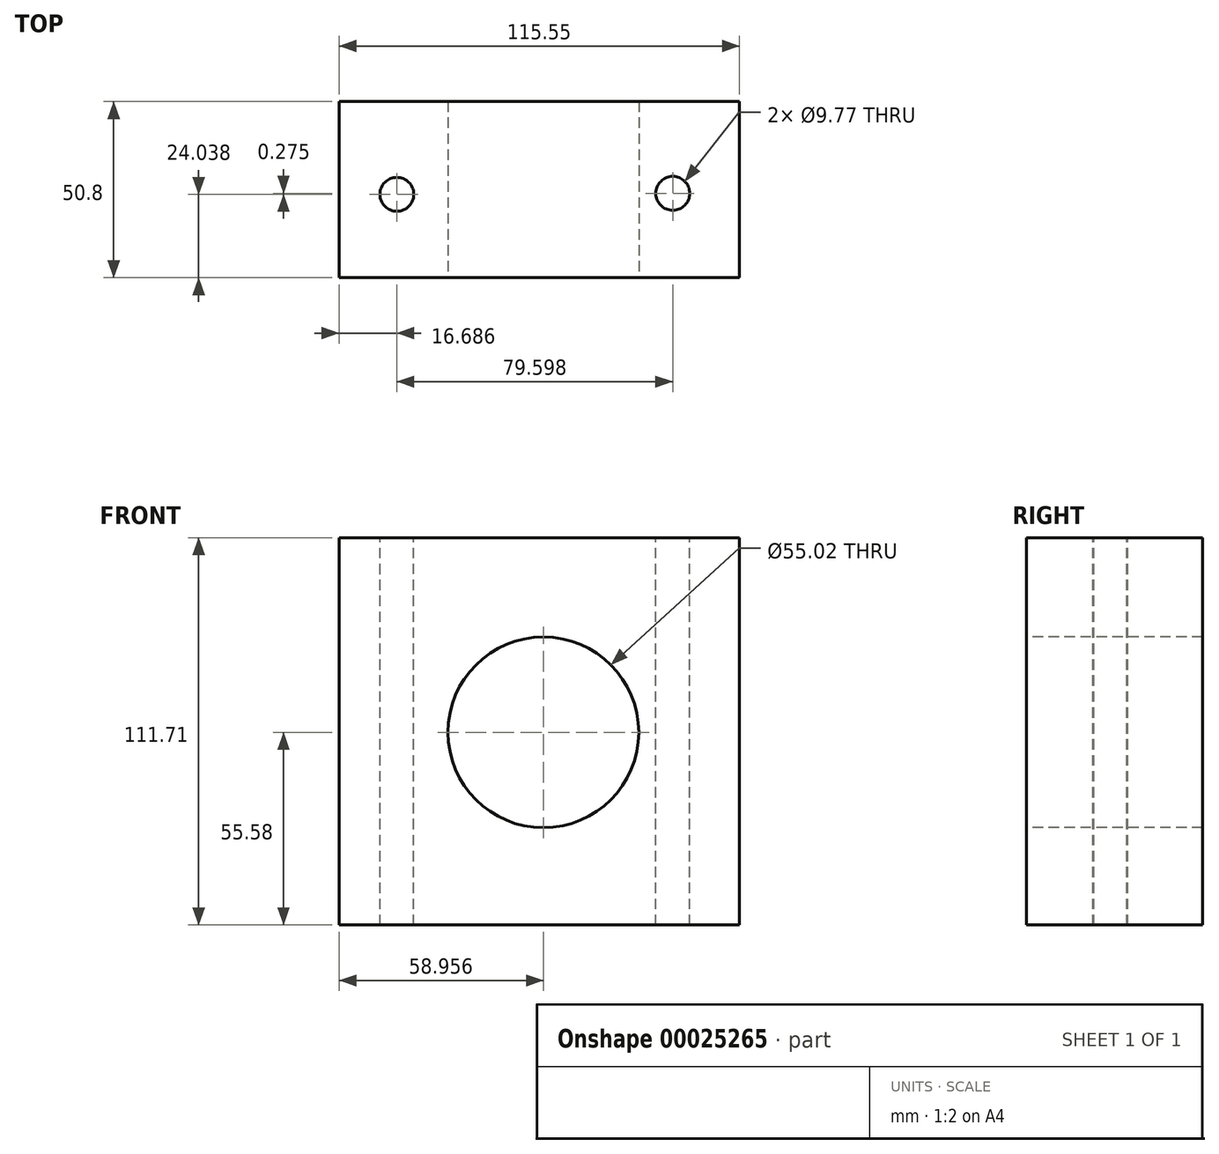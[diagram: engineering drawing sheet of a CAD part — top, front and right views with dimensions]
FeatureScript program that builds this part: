
annotation { "Feature Type Name" : "Feature", "Feature Type Description" : "" }
export const myFeature = defineFeature(function(context is Context, id is Id, definition is map)
    precondition{}
    {
        {
            var Q0;
            Q0=qCreatedBy(makeId("Front.planeOp"),FACE);
            var sketch = newSketch(context, id + "F0", { "sketchPlane" : qUnion([Q0])});
            skLineSegment(sketch, "E0", {"start": v(-76.3, 56.13) * mm, "end": v(-76.3, -55.58) * mm});
            skLineSegment(sketch, "E1", {"start": v(-76.3, -55.58) * mm, "end": v(39.25, -55.58) * mm});
            skLineSegment(sketch, "E2", {"start": v(39.25, -55.58) * mm, "end": v(39.25, 56.13) * mm});
            skLineSegment(sketch, "E3", {"start": v(39.25, 56.13) * mm, "end": v(-76.3, 56.13) * mm});
            skSolve(sketch);
        }
        {
            var Q0;
            Q0=makeQuery(id+"F0.imprint","IMPRINT",FACE,{"disambiguationData":[TD([[makeQuery(id+"F0.imprint","IMPRINT",EDGE,{"derivedFrom":sQuery(id+"F0.wireOp",EDGE,"E0")}),1.0]])]});
            extrude(context, id + "F1", {"entities" : qUnion([Q0]), "depth" : 50.8 * mm});
        }
        {
            var Q0;
            Q0=makeQuery(id+"F1.opExtrude","CAP_FACE",FACE,{"disambiguationData":[OSD([sQuery(id+"F0.wireOp",EDGE,"E0"),sQuery(id+"F0.wireOp",EDGE,"E1"),sQuery(id+"F0.wireOp",EDGE,"E2"),sQuery(id+"F0.wireOp",EDGE,"E3")])],"isStart":false});
            var sketch = newSketch(context, id + "F2", { "sketchPlane" : qUnion([Q0])});
            skCircle(sketch, "E4", {"center": v(-17.34, 0) * mm, "radius": 27.51 * mm});
            skSolve(sketch);
        }
        {
            var Q0;
            Q0=makeQuery(id+"F2.imprint","IMPRINT",FACE,{"disambiguationData":[TD([[makeQuery(id+"F2.imprint","IMPRINT",EDGE,{"derivedFrom":sQuery(id+"F2.wireOp",EDGE,"E4")}),1.0]])]});
            extrude(context, id + "F3", {"entities" : qUnion([Q0]), "operationType" : NewBodyOperationType.REMOVE, "endBound" : BoundingType.THROUGH_ALL, "oppositeDirection" : true, "depth" : 25.4 * mm});
        }
        {
            var Q0;
            Q0=makeQuery(id+"F1.opExtrude","SWEPT_FACE",FACE,{"disambiguationData":[OSD([sQuery(id+"F0.wireOp",EDGE,"E3")])]});
            var sketch = newSketch(context, id + "F4", { "sketchPlane" : qUnion([Q0])});
            skCircle(sketch, "E5", {"center": v(-59.61, -26.76) * mm, "radius": 4.89 * mm});
            skCircle(sketch, "E6", {"center": v(19.98, -26.49) * mm, "radius": 4.89 * mm});
            skSolve(sketch);
        }
        {
            var Q0;
            Q0=makeQuery(id+"F4.imprint","IMPRINT",FACE,{"disambiguationData":[TD([[makeQuery(id+"F4.imprint","IMPRINT",EDGE,{"derivedFrom":sQuery(id+"F4.wireOp",EDGE,"E5")}),1.0]])]});
            var Q1;
            Q1=makeQuery(id+"F4.imprint","IMPRINT",FACE,{"disambiguationData":[TD([[makeQuery(id+"F4.imprint","IMPRINT",EDGE,{"derivedFrom":sQuery(id+"F4.wireOp",EDGE,"E6")}),1.0]])]});
            extrude(context, id + "F5", {"entities" : qUnion([Q0, Q1]), "operationType" : NewBodyOperationType.REMOVE, "endBound" : BoundingType.THROUGH_ALL, "oppositeDirection" : true, "depth" : 25.4 * mm});
        }
    });
